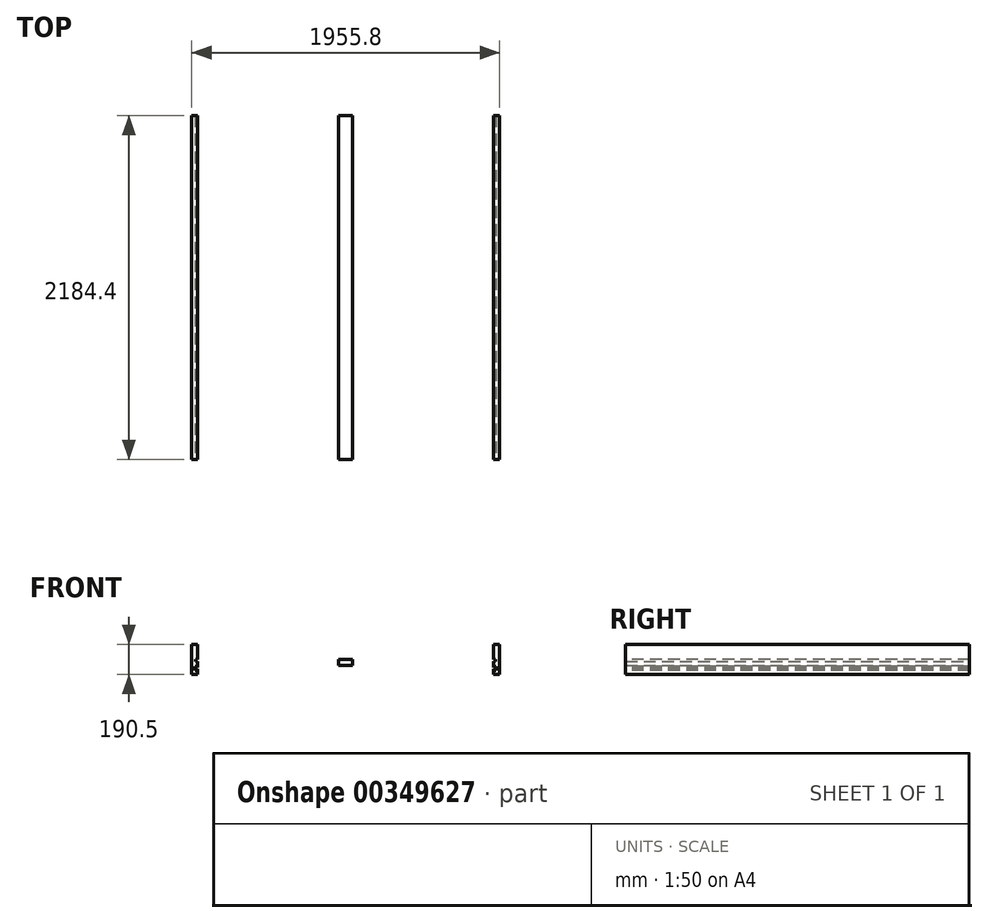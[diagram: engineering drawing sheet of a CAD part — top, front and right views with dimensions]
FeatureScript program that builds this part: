
annotation { "Feature Type Name" : "Feature", "Feature Type Description" : "" }
export const myFeature = defineFeature(function(context is Context, id is Id, definition is map)
    precondition{}
    {
        {
            var Q0;
            Q0=qCreatedBy(makeId("Front.planeOp"),FACE);
            var sketch = newSketch(context, id + "F0", { "sketchPlane" : qUnion([Q0])});
            skLineSegment(sketch, "E0.bottom", {"start": v(-939.8, -95.25) * mm, "end": v(-977.9, -95.25) * mm});
            skLineSegment(sketch, "E0.top", {"start": v(-939.8, 95.25) * mm, "end": v(-977.9, 95.25) * mm});
            skLineSegment(sketch, "E0.left", {"start": v(-939.8, -95.25) * mm, "end": v(-939.8, 95.25) * mm});
            skLineSegment(sketch, "E0.right", {"start": v(-977.9, -95.25) * mm, "end": v(-977.9, 95.25) * mm});
            skLineSegment(sketch, "E1.MirrorCS", {"start": v(977.9, -95.25) * mm, "end": v(977.9, 95.25) * mm});
            skLineSegment(sketch, "E2.MirrorCS", {"start": v(939.8, 95.25) * mm, "end": v(977.9, 95.25) * mm});
            skLineSegment(sketch, "E3.MirrorCS", {"start": v(939.8, -95.25) * mm, "end": v(939.8, 95.25) * mm});
            skLineSegment(sketch, "E4.MirrorCS", {"start": v(939.8, -95.25) * mm, "end": v(977.9, -95.25) * mm});
            skLineSegment(sketch, "E5.bottom", {"start": v(-44.45, 0) * mm, "end": v(44.45, 0) * mm});
            skLineSegment(sketch, "E5.top", {"start": v(-44.45, -38.1) * mm, "end": v(44.45, -38.1) * mm});
            skLineSegment(sketch, "E5.left", {"start": v(-44.45, 0) * mm, "end": v(-44.45, -38.1) * mm});
            skLineSegment(sketch, "E5.right", {"start": v(44.45, 0) * mm, "end": v(44.45, -38.1) * mm});
            skSolve(sketch);
        }
        {
            var Q0;
            Q0 = qSketchRegion(id + "F0", true);
            extrude(context, id + "F1", {"entities" : qUnion([Q0]), "endBound" : BoundingType.SYMMETRIC, "depth" : 2184.4 * mm});
        }
        {
            var Q0;
            Q0=qCreatedBy(makeId("Front.planeOp"),FACE);
            var sketch = newSketch(context, id + "F2", { "sketchPlane" : qUnion([Q0])});
            skLineSegment(sketch, "E6", {"start": v(-939.8, -61.91) * mm, "end": v(-949.32, -61.91) * mm});
            skLineSegment(sketch, "E7", {"start": v(-949.32, -61.91) * mm, "end": v(-949.32, -69.85) * mm});
            skLineSegment(sketch, "E8", {"start": v(-949.32, -69.85) * mm, "end": v(-955.67, -69.85) * mm});
            skLineSegment(sketch, "E9", {"start": v(-955.67, -69.85) * mm, "end": v(-955.67, -44.45) * mm});
            skLineSegment(sketch, "E10", {"start": v(-955.67, -44.45) * mm, "end": v(-949.32, -44.45) * mm});
            skLineSegment(sketch, "E11", {"start": v(-949.32, -44.45) * mm, "end": v(-949.32, -52.39) * mm});
            skLineSegment(sketch, "E12", {"start": v(-949.32, -52.39) * mm, "end": v(-939.8, -52.39) * mm});
            skLineSegment(sketch, "E13", {"start": v(-939.8, -52.39) * mm, "end": v(-939.8, -61.91) * mm});
            skLineSegment(sketch, "E14", {"start": v(-939.8, -57.15) * mm, "end": v(-955.67, -57.15) * mm});
            skLineSegment(sketch, "E15.MirrorCS", {"start": v(939.8, -52.39) * mm, "end": v(939.8, -61.91) * mm});
            skLineSegment(sketch, "E16.MirrorCS", {"start": v(949.32, -61.91) * mm, "end": v(949.32, -69.85) * mm});
            skLineSegment(sketch, "E17.MirrorCS", {"start": v(949.32, -69.85) * mm, "end": v(955.67, -69.85) * mm});
            skLineSegment(sketch, "E18.MirrorCS", {"start": v(939.8, -61.91) * mm, "end": v(949.32, -61.91) * mm});
            skLineSegment(sketch, "E19.MirrorCS", {"start": v(949.32, -44.45) * mm, "end": v(949.32, -52.39) * mm});
            skLineSegment(sketch, "E20.MirrorCS", {"start": v(955.67, -69.85) * mm, "end": v(955.67, -44.45) * mm});
            skLineSegment(sketch, "E21.MirrorCS", {"start": v(955.67, -44.45) * mm, "end": v(949.32, -44.45) * mm});
            skLineSegment(sketch, "E22.MirrorCS", {"start": v(949.32, -52.39) * mm, "end": v(939.8, -52.39) * mm});
            skLineSegment(sketch, "E23.MirrorCS", {"start": v(939.8, -57.15) * mm, "end": v(955.67, -57.15) * mm});
            skLineSegment(sketch, "E24.bottom", {"start": v(-939.8, -12.7) * mm, "end": v(-952.5, -12.7) * mm});
            skLineSegment(sketch, "E24.top", {"start": v(-939.8, 0) * mm, "end": v(-952.5, 0) * mm});
            skLineSegment(sketch, "E24.left", {"start": v(-939.8, -12.7) * mm, "end": v(-939.8, 0) * mm});
            skLineSegment(sketch, "E24.right", {"start": v(-952.5, -12.7) * mm, "end": v(-952.5, 0) * mm});
            skLineSegment(sketch, "E25.MirrorCS", {"start": v(952.5, -12.7) * mm, "end": v(952.5, 0) * mm});
            skLineSegment(sketch, "E26.MirrorCS", {"start": v(939.8, -12.7) * mm, "end": v(939.8, 0) * mm});
            skLineSegment(sketch, "E27.MirrorCS", {"start": v(939.8, 0) * mm, "end": v(952.5, 0) * mm});
            skLineSegment(sketch, "E28.MirrorCS", {"start": v(939.8, -12.7) * mm, "end": v(952.5, -12.7) * mm});
            skSolve(sketch);
        }
        {
            var Q0;
            Q0 = qSketchRegion(id + "F2", true);
            var Q1;
            Q1 = qSketchRegion(id + "F4", true);
            extrude(context, id + "F3", {"entities" : qUnion([Q0, Q1]), "operationType" : NewBodyOperationType.REMOVE, "endBound" : BoundingType.SYMMETRIC, "oppositeDirection" : true, "depth" : 2184.4 * mm});
        }
        {
            var Q0;
            Q0=qCreatedBy(makeId("Front.planeOp"),FACE);
            var sketch = newSketch(context, id + "F4", { "sketchPlane" : qUnion([Q0])});
            skLineSegment(sketch, "E29.bottom", {"start": v(-952.5, 0) * mm, "end": v(-914.4, 0) * mm});
            skLineSegment(sketch, "E29.top", {"start": v(-952.5, -19.05) * mm, "end": v(-914.4, -19.05) * mm});
            skLineSegment(sketch, "E29.left", {"start": v(-952.5, 0) * mm, "end": v(-952.5, -19.05) * mm});
            skLineSegment(sketch, "E29.right", {"start": v(-914.4, 0) * mm, "end": v(-914.4, -19.05) * mm});
            skLineSegment(sketch, "E30.MirrorCS", {"start": v(952.5, 0) * mm, "end": v(914.4, 0) * mm});
            skLineSegment(sketch, "E31.MirrorCS", {"start": v(952.5, -19.05) * mm, "end": v(914.4, -19.05) * mm});
            skLineSegment(sketch, "E32.MirrorCS", {"start": v(952.5, 0) * mm, "end": v(952.5, -19.05) * mm});
            skLineSegment(sketch, "E33.MirrorCS", {"start": v(914.4, 0) * mm, "end": v(914.4, -19.05) * mm});
            skSolve(sketch);
        }
    });
